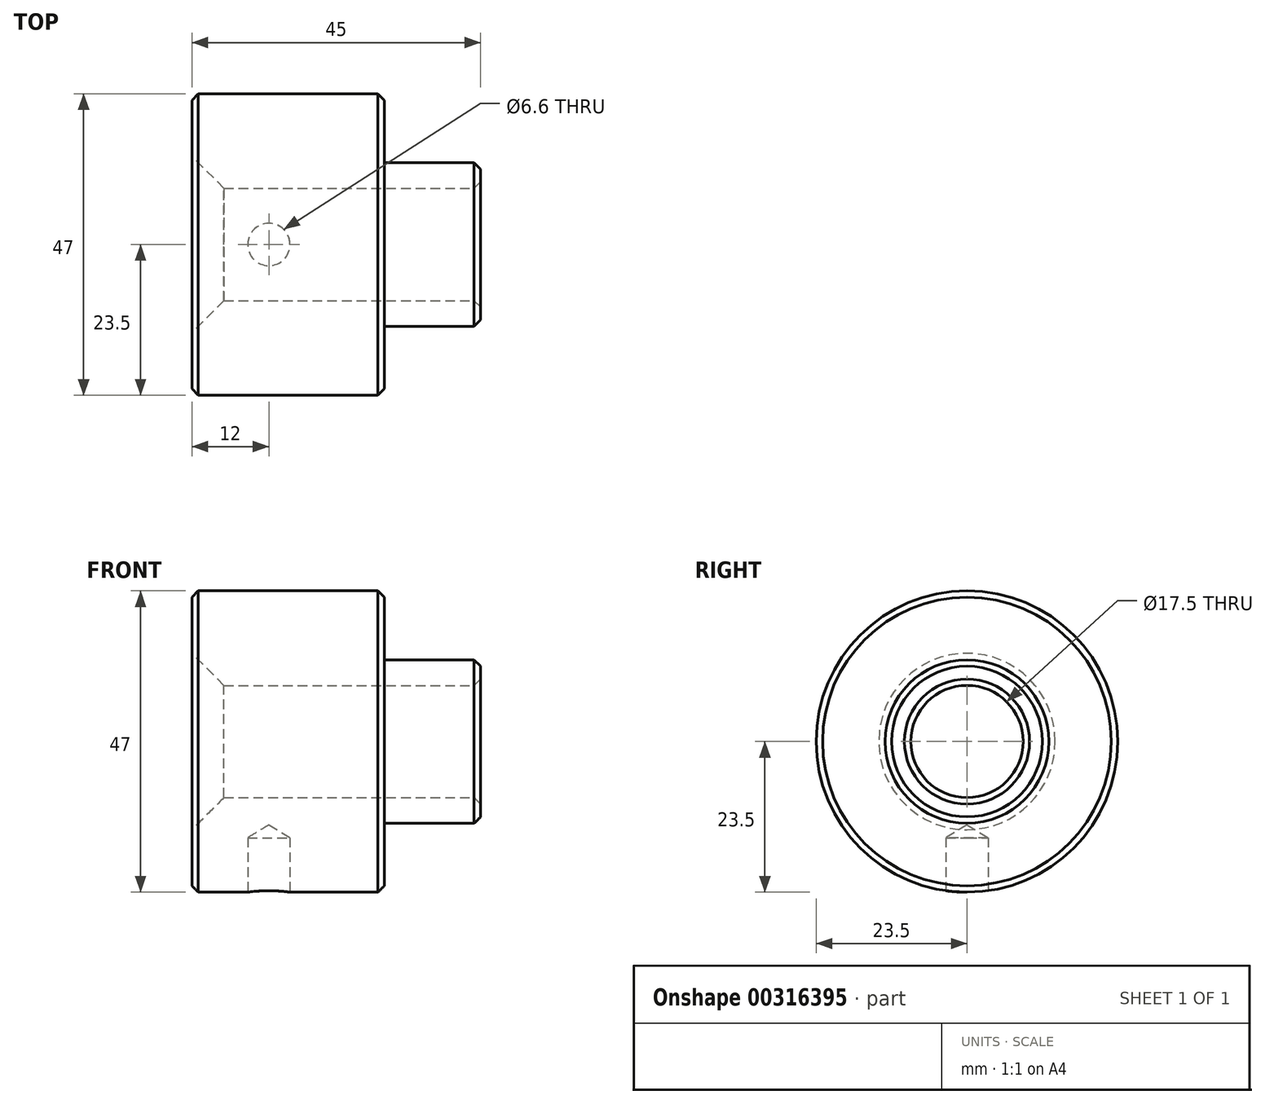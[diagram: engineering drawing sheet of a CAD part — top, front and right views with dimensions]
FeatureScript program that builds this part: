
annotation { "Feature Type Name" : "Feature", "Feature Type Description" : "" }
export const myFeature = defineFeature(function(context is Context, id is Id, definition is map)
    precondition{}
    {
        {
            var Q0;
            Q0=qCreatedBy(makeId("Front.planeOp"),FACE);
            var sketch = newSketch(context, id + "F0", { "sketchPlane" : qUnion([Q0])});
            skLineSegment(sketch, "E0.bottom", {"start": v(0, 8.75) * mm, "end": v(-30, 8.75) * mm});
            skLineSegment(sketch, "E0.top", {"start": v(0, 23.5) * mm, "end": v(-30, 23.5) * mm});
            skLineSegment(sketch, "E0.left", {"start": v(0, 8.75) * mm, "end": v(0, 23.5) * mm});
            skLineSegment(sketch, "E0.right", {"start": v(-30, 8.75) * mm, "end": v(-30, 23.5) * mm});
            skLineSegment(sketch, "E1.bottom", {"start": v(0, 8.75) * mm, "end": v(15, 8.75) * mm});
            skLineSegment(sketch, "E1.top", {"start": v(0, 12.75) * mm, "end": v(15, 12.75) * mm});
            skLineSegment(sketch, "E1.left", {"start": v(0, 8.75) * mm, "end": v(0, 12.75) * mm});
            skLineSegment(sketch, "E1.right", {"start": v(15, 8.75) * mm, "end": v(15, 12.75) * mm});
            skLineSegment(sketch, "E2", {"start": v(0, 0) * mm, "end": v(-38.5, 0) * mm});
            skSolve(sketch);
        }
        {
            var Q0;
            Q0 = qSketchRegion(id + "F0", true);
            var Q1;
            Q1=sQuery(id+"F0.wireOp",EDGE,"E2");
            revolve(context, id + "F1", {"entities" : qUnion([Q0]), "axis" : qUnion([Q1]), "revolveType" : RevolveType.FULL});
        }
        {
            var Q0;
            Q0=qCreatedBy(makeId("Top.planeOp"),FACE);
            var sketch = newSketch(context, id + "F2", { "sketchPlane" : qUnion([Q0])});
            skCircle(sketch, "E3", {"center": v(-18, 0) * mm, "radius": 3 * mm});
            skSolve(sketch);
        }
        {
            var Q0;
            Q0=makeQuery(id+"F1.opRevolve","SWEPT_EDGE",EDGE,{"disambiguationData":[OSD([sQuery(id+"F0.wireOp",EDGE,"E0.bottom"),sQuery(id+"F0.wireOp",EDGE,"E0.right")])]});
            chamfer(context, id + "F3", {"entities" : qUnion([Q0]), "width" : 5 * mm, "tangentPropagation" : true});
        }
        {
            var Q0;
            Q0=qCreatedBy(makeId("Top.planeOp"),FACE);
            cPlane(context, id + "F4", {"entities" : qUnion([Q0]), "cplaneType" : CPlaneType.OFFSET, "offset" : 25 * mm, "oppositeDirection" : true, "width" : 150 * mm, "height" : 150 * mm});
        }
        {
            var Q0;
            Q0=qCreatedBy(id+"F4.planeOp",FACE);
            var sketch = newSketch(context, id + "F5", { "sketchPlane" : qUnion([Q0])});
            skLineSegment(sketch, "E4", {"start": v(-30, 0) * mm, "end": v(-18, 0) * mm, "construction": true});
            skSolve(sketch);
        }
        {
            var Q0;
            Q0=sQuery(id+"F5.wireOp",VERTEX,"E4.end");
            var Q1;
            Q1=makeQuery(id+"F1.opRevolve","SWEPT_BODY",BODY,{"disambiguationData":[OSD([sQuery(id+"F0.wireOp",EDGE,"E0.bottom"),sQuery(id+"F0.wireOp",EDGE,"E0.top"),sQuery(id+"F0.wireOp",EDGE,"E0.left"),sQuery(id+"F0.wireOp",EDGE,"E0.right"),sQuery(id+"F0.wireOp",EDGE,"E1.bottom"),sQuery(id+"F0.wireOp",EDGE,"E1.top"),sQuery(id+"F0.wireOp",EDGE,"E1.right")])]});
            hole(context, id + "F6", {"style" : HoleStyle.SIMPLE, "endStyle" : HoleEndStyle.BLIND, "oppositeDirection" : true, "standardTappedOrClearance" : lookupTablePath({ "standard" : "ISO", "fit" : "Normal", "size" : "M6", "type" : "Clearance" }), "standardBlindInLast" : lookupTablePath({ "fit" : "Standard", "standard" : "ISO", "size" : "M6", "type" : "Clearance" }), "holeDiameter" : 6.6 * mm, "majorDiameter" : 5 * mm, "holeDepth" : 10 * mm, "isTappedThrough" : true, "tappedDepth" : 37.5 * mm, "tapClearance" : 3, "startFromSketch" : true, "locations" : qUnion([Q0]), "scope" : qUnion([Q1])});
        }
        {
            var Q0;
            Q0=makeQuery(id+"F1.opRevolve","SWEPT_EDGE",EDGE,{"disambiguationData":[OSD([sQuery(id+"F0.wireOp",EDGE,"E0.top"),sQuery(id+"F0.wireOp",EDGE,"E0.right")])]});
            var Q1;
            Q1=makeQuery(id+"F1.opRevolve","SWEPT_EDGE",EDGE,{"disambiguationData":[OSD([sQuery(id+"F0.wireOp",EDGE,"E0.top"),sQuery(id+"F0.wireOp",EDGE,"E0.left")])]});
            var Q2;
            Q2=makeQuery(id+"F1.opRevolve","SWEPT_EDGE",EDGE,{"disambiguationData":[OSD([sQuery(id+"F0.wireOp",EDGE,"E1.top"),sQuery(id+"F0.wireOp",EDGE,"E1.right")])]});
            var Q3;
            Q3=makeQuery(id+"F1.opRevolve","SWEPT_EDGE",EDGE,{"disambiguationData":[OSD([sQuery(id+"F0.wireOp",EDGE,"E1.bottom"),sQuery(id+"F0.wireOp",EDGE,"E1.right")])]});
            chamfer(context, id + "F7", {"entities" : qUnion([Q0, Q1, Q2, Q3]), "width" : 1 * mm, "tangentPropagation" : true});
        }
    });
